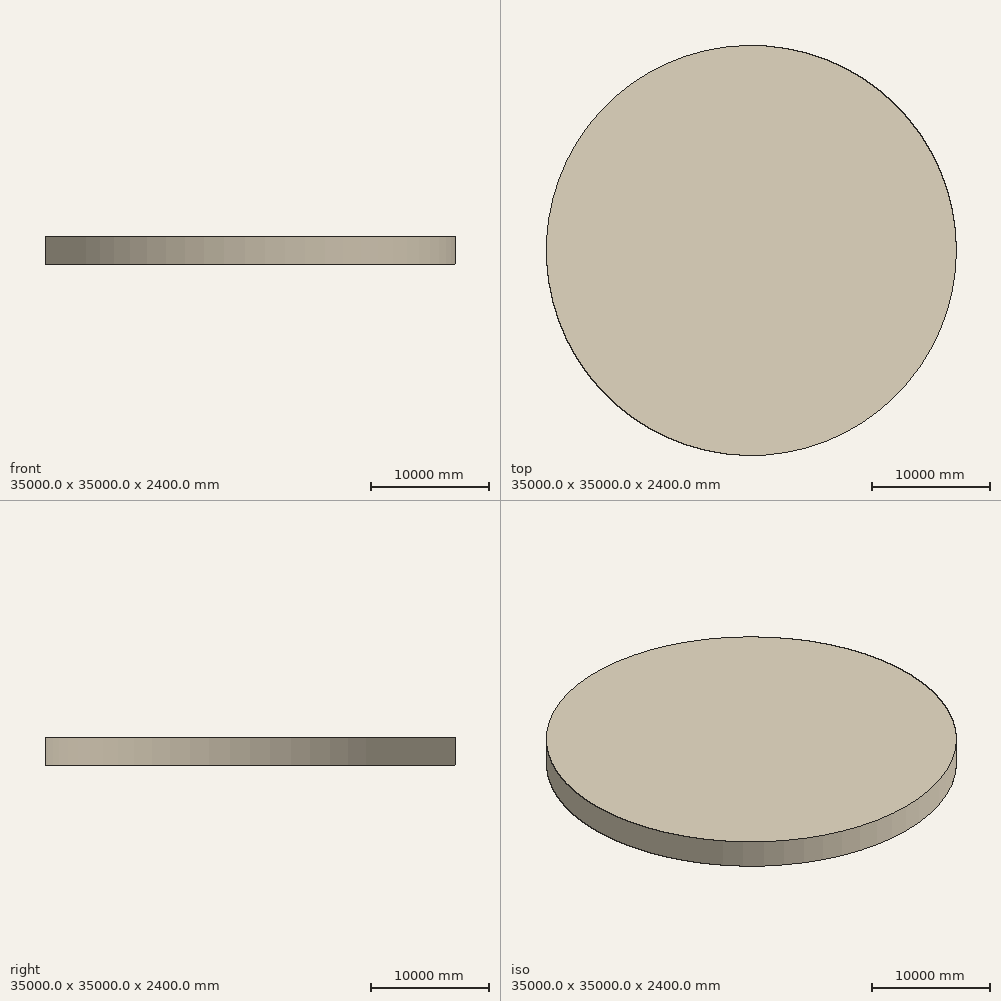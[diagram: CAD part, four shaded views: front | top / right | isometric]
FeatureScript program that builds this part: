
annotation { "Feature Type Name" : "Feature", "Feature Type Description" : "" }
export const myFeature = defineFeature(function(context is Context, id is Id, definition is map)
    precondition{}
    {
        {
            var Q0;
            Q0=qCreatedBy(makeId("Top.planeOp"),FACE);
            var sketch = newSketch(context, id + "F0", { "sketchPlane" : qUnion([Q0])});
            skCircle(sketch, "E0", {"center": v(0, 0) * mm, "radius": 17500 * mm});
            skSolve(sketch);
        }
        {
            var Q0;
            Q0=makeQuery(id+"F0.imprint","IMPRINT",FACE,{"disambiguationData":[TD([[makeQuery(id+"F0.imprint","IMPRINT",EDGE,{"derivedFrom":sQuery(id+"F0.wireOp",EDGE,"E0")}),1.0]])]});
            extrude(context, id + "F1", {"entities" : qUnion([Q0]), "depth" : 2400 * mm});
        }
    });
